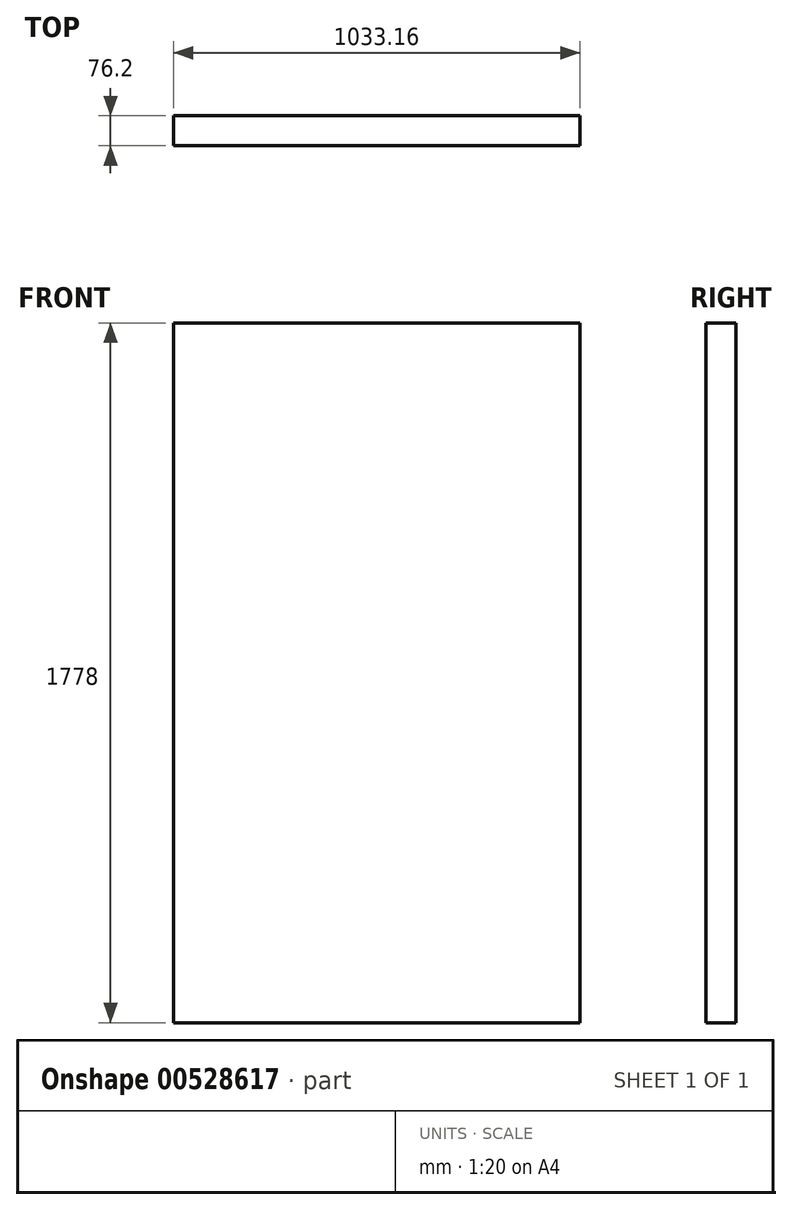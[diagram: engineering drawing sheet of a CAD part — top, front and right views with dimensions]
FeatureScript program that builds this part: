
annotation { "Feature Type Name" : "Feature", "Feature Type Description" : "" }
export const myFeature = defineFeature(function(context is Context, id is Id, definition is map)
    precondition{}
    {
        {
            var Q0;
            Q0=qCreatedBy(makeId("Front.planeOp"),FACE);
            var sketch = newSketch(context, id + "F0", { "sketchPlane" : qUnion([Q0])});
            skLineSegment(sketch, "E0.bottom", {"start": v(-516.96, 889.38) * mm, "end": v(516.2, 889.38) * mm});
            skLineSegment(sketch, "E0.top", {"start": v(-516.96, -888.62) * mm, "end": v(516.2, -888.62) * mm});
            skLineSegment(sketch, "E0.left", {"start": v(-516.96, 889.38) * mm, "end": v(-516.96, -888.62) * mm});
            skLineSegment(sketch, "E0.right", {"start": v(516.2, 889.38) * mm, "end": v(516.2, -888.62) * mm});
            skSolve(sketch);
        }
        {
            var Q0;
            Q0=makeQuery(id+"F0.imprint","IMPRINT",FACE,{"disambiguationData":[TD([[makeQuery(id+"F0.imprint","IMPRINT",EDGE,{"derivedFrom":sQuery(id+"F0.wireOp",EDGE,"E0.bottom")}),-1.0]])]});
            extrude(context, id + "F1", {"entities" : qUnion([Q0]), "depth" : 76.2 * mm, "offsetDistance" : 25.4 * mm});
        }
    });
